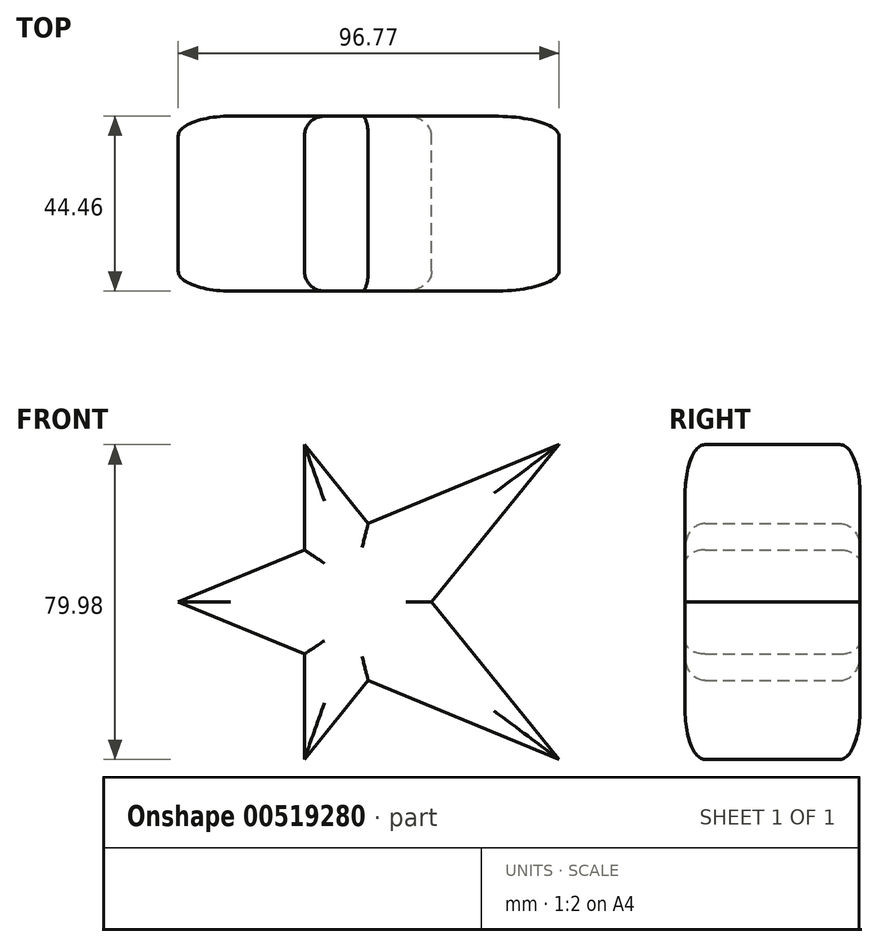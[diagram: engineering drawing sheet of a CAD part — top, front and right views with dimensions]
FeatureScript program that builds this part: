
annotation { "Feature Type Name" : "Feature", "Feature Type Description" : "" }
export const myFeature = defineFeature(function(context is Context, id is Id, definition is map)
    precondition{}
    {
        {
            var Q0;
            Q0=qCreatedBy(makeId("Front.planeOp"),FACE);
            var sketch = newSketch(context, id + "F0", { "sketchPlane" : qUnion([Q0])});
            skLineSegment(sketch, "E0", {"start": v(-48.54, 0) * mm, "end": v(48.23, 40) * mm});
            skLineSegment(sketch, "E1.MirrorCS", {"start": v(-48.54, 0) * mm, "end": v(48.23, -40) * mm});
            skLineSegment(sketch, "E2", {"start": v(-16.48, 40) * mm, "end": v(48.23, -40) * mm});
            skLineSegment(sketch, "E3", {"start": v(48.23, 40) * mm, "end": v(-16.48, -40) * mm});
            skLineSegment(sketch, "E4", {"start": v(-16.48, 40) * mm, "end": v(-16.48, -40) * mm});
            skSolve(sketch);
        }
        {
            var Q0;
            {var subQ5=sQuery(id+"F0.wireOp",EDGE,"E0");var subQ7=sQuery(id+"F0.wireOp",EDGE,"E4");var subQ9=makeQuery(id+"F0.imprint","INTERSECT",VERTEX,{"derivedFrom":[subQ5,subQ7]});Q0=makeQuery(id+"F0.imprint","IMPRINT",FACE,{"disambiguationData":[TD([[makeQuery(id+"F0.imprint","IMPRINT",EDGE,{"disambiguationData":[TD([[subQ9,-1.0]])],"derivedFrom":subQ5}),-1.0]])]});}
            var Q1;
            {var subQ0=sQuery(id+"F0.wireOp",EDGE,"E1.MirrorCS");var subQ1=sQuery(id+"F0.wireOp",EDGE,"E0");var subQ2=makeQuery(id+"F0.imprint","INTERSECT",VERTEX,{"derivedFrom":[subQ1,subQ0]});Q1=makeQuery(id+"F0.imprint","IMPRINT",FACE,{"disambiguationData":[TD([[makeQuery(id+"F0.imprint","IMPRINT",EDGE,{"disambiguationData":[TD([[subQ2,-1.0]])],"derivedFrom":subQ1}),-1.0]])]});}
            var Q2;
            {var subQ0=sQuery(id+"F0.wireOp",EDGE,"E4");var subQ1=sQuery(id+"F0.wireOp",EDGE,"E0");var subQ2=makeQuery(id+"F0.imprint","INTERSECT",VERTEX,{"derivedFrom":[subQ1,subQ0]});Q2=makeQuery(id+"F0.imprint","IMPRINT",FACE,{"disambiguationData":[TD([[makeQuery(id+"F0.imprint","IMPRINT",EDGE,{"disambiguationData":[TD([[subQ2,-1.0]])],"derivedFrom":subQ1}),1.0]])]});}
            var Q3;
            {var subQ0=sQuery(id+"F0.wireOp",EDGE,"E3");var subQ1=sQuery(id+"F0.wireOp",EDGE,"E0");var subQ2=makeQuery(id+"F0.imprint","INTERSECT",VERTEX,{"derivedFrom":[subQ1,subQ0]});Q3=makeQuery(id+"F0.imprint","IMPRINT",FACE,{"disambiguationData":[TD([[makeQuery(id+"F0.imprint","IMPRINT",EDGE,{"disambiguationData":[TD([[subQ2,1.0]])],"derivedFrom":subQ1}),-1.0]])]});}
            var Q4;
            {var subQ0=sQuery(id+"F0.wireOp",EDGE,"E2");var subQ1=sQuery(id+"F0.wireOp",EDGE,"E1.MirrorCS");var subQ2=makeQuery(id+"F0.imprint","INTERSECT",VERTEX,{"derivedFrom":[subQ1,subQ0]});Q4=makeQuery(id+"F0.imprint","IMPRINT",FACE,{"disambiguationData":[TD([[makeQuery(id+"F0.imprint","IMPRINT",EDGE,{"disambiguationData":[TD([[subQ2,1.0]])],"derivedFrom":subQ1}),1.0]])]});}
            var Q5;
            {var subQ0=sQuery(id+"F0.wireOp",EDGE,"E4");var subQ1=sQuery(id+"F0.wireOp",EDGE,"E1.MirrorCS");var subQ2=makeQuery(id+"F0.imprint","INTERSECT",VERTEX,{"derivedFrom":[subQ1,subQ0]});Q5=makeQuery(id+"F0.imprint","IMPRINT",FACE,{"disambiguationData":[TD([[makeQuery(id+"F0.imprint","IMPRINT",EDGE,{"disambiguationData":[TD([[subQ2,-1.0]])],"derivedFrom":subQ1}),-1.0]])]});}
            extrude(context, id + "F1", {"entities" : qUnion([Q0, Q1, Q2, Q3, Q4, Q5]), "endBound" : BoundingType.SYMMETRIC, "depth" : 44.45 * mm, "offsetDistance" : 25.4 * mm});
        }
        {
            var Q0;
            {var subQ0=sQuery(id+"F0.wireOp",EDGE,"E1.MirrorCS");Q0=makeQuery(id+"F1.opExtrude","CAP_EDGE",EDGE,{"disambiguationData":[OSD([subQ0]),TDD([makeQuery(id+"F0.imprint","IMPRINT",EDGE,{"disambiguationData":[TD([[makeQuery(id+"F0.imprint","INTERSECT",VERTEX,{"derivedFrom":[sQuery(id+"F0.wireOp",EDGE,"E0"),subQ0]}),-1.0]])],"derivedFrom":subQ0})])],"isStart":false});}
            var Q1;
            {var subQ0=sQuery(id+"F0.wireOp",EDGE,"E4");Q1=makeQuery(id+"F1.opExtrude","CAP_EDGE",EDGE,{"disambiguationData":[OSD([subQ0]),TDD([makeQuery(id+"F0.imprint","IMPRINT",EDGE,{"disambiguationData":[TD([[makeQuery(id+"F0.imprint","INTERSECT",VERTEX,{"derivedFrom":[sQuery(id+"F0.wireOp",EDGE,"E3"),subQ0]}),1.0]])],"derivedFrom":subQ0})])],"isStart":false});}
            var Q2;
            {var subQ0=sQuery(id+"F0.wireOp",EDGE,"E3");Q2=makeQuery(id+"F1.opExtrude","CAP_EDGE",EDGE,{"disambiguationData":[OSD([subQ0]),TDD([makeQuery(id+"F0.imprint","IMPRINT",EDGE,{"disambiguationData":[TD([[makeQuery(id+"F0.imprint","INTERSECT",VERTEX,{"derivedFrom":[subQ0,sQuery(id+"F0.wireOp",EDGE,"E4")]}),1.0]])],"derivedFrom":subQ0})])],"isStart":false});}
            var Q3;
            {var subQ0=sQuery(id+"F0.wireOp",EDGE,"E1.MirrorCS");Q3=makeQuery(id+"F1.opExtrude","CAP_EDGE",EDGE,{"disambiguationData":[OSD([subQ0]),TDD([makeQuery(id+"F0.imprint","IMPRINT",EDGE,{"disambiguationData":[TD([[makeQuery(id+"F0.imprint","INTERSECT",VERTEX,{"derivedFrom":[subQ0,sQuery(id+"F0.wireOp",EDGE,"E2")]}),1.0]])],"derivedFrom":subQ0})])],"isStart":false});}
            var Q4;
            {var subQ0=sQuery(id+"F0.wireOp",EDGE,"E2");Q4=makeQuery(id+"F1.opExtrude","CAP_EDGE",EDGE,{"disambiguationData":[OSD([subQ0]),TDD([makeQuery(id+"F0.imprint","IMPRINT",EDGE,{"disambiguationData":[TD([[makeQuery(id+"F0.imprint","INTERSECT",VERTEX,{"derivedFrom":[sQuery(id+"F0.wireOp",EDGE,"E1.MirrorCS"),subQ0]}),1.0]])],"derivedFrom":subQ0})])],"isStart":false});}
            var Q5;
            {var subQ0=sQuery(id+"F0.wireOp",EDGE,"E3");Q5=makeQuery(id+"F1.opExtrude","CAP_EDGE",EDGE,{"disambiguationData":[OSD([subQ0]),TDD([makeQuery(id+"F0.imprint","IMPRINT",EDGE,{"disambiguationData":[TD([[makeQuery(id+"F0.imprint","INTERSECT",VERTEX,{"derivedFrom":[sQuery(id+"F0.wireOp",EDGE,"E0"),subQ0]}),-1.0]])],"derivedFrom":subQ0})])],"isStart":false});}
            var Q6;
            {var subQ0=sQuery(id+"F0.wireOp",EDGE,"E0");Q6=makeQuery(id+"F1.opExtrude","CAP_EDGE",EDGE,{"disambiguationData":[OSD([subQ0]),TDD([makeQuery(id+"F0.imprint","IMPRINT",EDGE,{"disambiguationData":[TD([[makeQuery(id+"F0.imprint","INTERSECT",VERTEX,{"derivedFrom":[subQ0,sQuery(id+"F0.wireOp",EDGE,"E3")]}),1.0]])],"derivedFrom":subQ0})])],"isStart":false});}
            var Q7;
            {var subQ0=sQuery(id+"F0.wireOp",EDGE,"E2");Q7=makeQuery(id+"F1.opExtrude","CAP_EDGE",EDGE,{"disambiguationData":[OSD([subQ0]),TDD([makeQuery(id+"F0.imprint","IMPRINT",EDGE,{"disambiguationData":[TD([[makeQuery(id+"F0.imprint","INTERSECT",VERTEX,{"derivedFrom":[subQ0,sQuery(id+"F0.wireOp",EDGE,"E4")]}),-1.0]])],"derivedFrom":subQ0})])],"isStart":false});}
            var Q8;
            {var subQ0=sQuery(id+"F0.wireOp",EDGE,"E4");Q8=makeQuery(id+"F1.opExtrude","CAP_EDGE",EDGE,{"disambiguationData":[OSD([subQ0]),TDD([makeQuery(id+"F0.imprint","IMPRINT",EDGE,{"disambiguationData":[TD([[makeQuery(id+"F0.imprint","INTERSECT",VERTEX,{"derivedFrom":[sQuery(id+"F0.wireOp",EDGE,"E2"),subQ0]}),-1.0]])],"derivedFrom":subQ0})])],"isStart":false});}
            var Q9;
            {var subQ0=sQuery(id+"F0.wireOp",EDGE,"E0");Q9=makeQuery(id+"F1.opExtrude","CAP_EDGE",EDGE,{"disambiguationData":[OSD([subQ0]),TDD([makeQuery(id+"F0.imprint","IMPRINT",EDGE,{"disambiguationData":[TD([[makeQuery(id+"F0.imprint","INTERSECT",VERTEX,{"derivedFrom":[subQ0,sQuery(id+"F0.wireOp",EDGE,"E1.MirrorCS")]}),-1.0]])],"derivedFrom":subQ0})])],"isStart":false});}
            var Q10;
            {var subQ0=sQuery(id+"F0.wireOp",EDGE,"E0");Q10=makeQuery(id+"F1.opExtrude","CAP_EDGE",EDGE,{"disambiguationData":[OSD([subQ0]),TDD([makeQuery(id+"F0.imprint","IMPRINT",EDGE,{"disambiguationData":[TD([[makeQuery(id+"F0.imprint","INTERSECT",VERTEX,{"derivedFrom":[subQ0,sQuery(id+"F0.wireOp",EDGE,"E1.MirrorCS")]}),-1.0]])],"derivedFrom":subQ0})])],"isStart":true});}
            var Q11;
            {var subQ0=sQuery(id+"F0.wireOp",EDGE,"E4");Q11=makeQuery(id+"F1.opExtrude","CAP_EDGE",EDGE,{"disambiguationData":[OSD([subQ0]),TDD([makeQuery(id+"F0.imprint","IMPRINT",EDGE,{"disambiguationData":[TD([[makeQuery(id+"F0.imprint","INTERSECT",VERTEX,{"derivedFrom":[sQuery(id+"F0.wireOp",EDGE,"E2"),subQ0]}),-1.0]])],"derivedFrom":subQ0})])],"isStart":true});}
            var Q12;
            {var subQ0=sQuery(id+"F0.wireOp",EDGE,"E2");Q12=makeQuery(id+"F1.opExtrude","CAP_EDGE",EDGE,{"disambiguationData":[OSD([subQ0]),TDD([makeQuery(id+"F0.imprint","IMPRINT",EDGE,{"disambiguationData":[TD([[makeQuery(id+"F0.imprint","INTERSECT",VERTEX,{"derivedFrom":[subQ0,sQuery(id+"F0.wireOp",EDGE,"E4")]}),-1.0]])],"derivedFrom":subQ0})])],"isStart":true});}
            var Q13;
            {var subQ0=sQuery(id+"F0.wireOp",EDGE,"E0");Q13=makeQuery(id+"F1.opExtrude","CAP_EDGE",EDGE,{"disambiguationData":[OSD([subQ0]),TDD([makeQuery(id+"F0.imprint","IMPRINT",EDGE,{"disambiguationData":[TD([[makeQuery(id+"F0.imprint","INTERSECT",VERTEX,{"derivedFrom":[subQ0,sQuery(id+"F0.wireOp",EDGE,"E3")]}),1.0]])],"derivedFrom":subQ0})])],"isStart":true});}
            var Q14;
            {var subQ0=sQuery(id+"F0.wireOp",EDGE,"E3");Q14=makeQuery(id+"F1.opExtrude","CAP_EDGE",EDGE,{"disambiguationData":[OSD([subQ0]),TDD([makeQuery(id+"F0.imprint","IMPRINT",EDGE,{"disambiguationData":[TD([[makeQuery(id+"F0.imprint","INTERSECT",VERTEX,{"derivedFrom":[sQuery(id+"F0.wireOp",EDGE,"E0"),subQ0]}),-1.0]])],"derivedFrom":subQ0})])],"isStart":true});}
            var Q15;
            {var subQ0=sQuery(id+"F0.wireOp",EDGE,"E2");Q15=makeQuery(id+"F1.opExtrude","CAP_EDGE",EDGE,{"disambiguationData":[OSD([subQ0]),TDD([makeQuery(id+"F0.imprint","IMPRINT",EDGE,{"disambiguationData":[TD([[makeQuery(id+"F0.imprint","INTERSECT",VERTEX,{"derivedFrom":[sQuery(id+"F0.wireOp",EDGE,"E1.MirrorCS"),subQ0]}),1.0]])],"derivedFrom":subQ0})])],"isStart":true});}
            var Q16;
            {var subQ0=sQuery(id+"F0.wireOp",EDGE,"E1.MirrorCS");Q16=makeQuery(id+"F1.opExtrude","CAP_EDGE",EDGE,{"disambiguationData":[OSD([subQ0]),TDD([makeQuery(id+"F0.imprint","IMPRINT",EDGE,{"disambiguationData":[TD([[makeQuery(id+"F0.imprint","INTERSECT",VERTEX,{"derivedFrom":[subQ0,sQuery(id+"F0.wireOp",EDGE,"E2")]}),1.0]])],"derivedFrom":subQ0})])],"isStart":true});}
            var Q17;
            {var subQ0=sQuery(id+"F0.wireOp",EDGE,"E3");Q17=makeQuery(id+"F1.opExtrude","CAP_EDGE",EDGE,{"disambiguationData":[OSD([subQ0]),TDD([makeQuery(id+"F0.imprint","IMPRINT",EDGE,{"disambiguationData":[TD([[makeQuery(id+"F0.imprint","INTERSECT",VERTEX,{"derivedFrom":[subQ0,sQuery(id+"F0.wireOp",EDGE,"E4")]}),1.0]])],"derivedFrom":subQ0})])],"isStart":true});}
            var Q18;
            {var subQ0=sQuery(id+"F0.wireOp",EDGE,"E4");Q18=makeQuery(id+"F1.opExtrude","CAP_EDGE",EDGE,{"disambiguationData":[OSD([subQ0]),TDD([makeQuery(id+"F0.imprint","IMPRINT",EDGE,{"disambiguationData":[TD([[makeQuery(id+"F0.imprint","INTERSECT",VERTEX,{"derivedFrom":[sQuery(id+"F0.wireOp",EDGE,"E3"),subQ0]}),1.0]])],"derivedFrom":subQ0})])],"isStart":true});}
            var Q19;
            {var subQ0=sQuery(id+"F0.wireOp",EDGE,"E1.MirrorCS");Q19=makeQuery(id+"F1.opExtrude","CAP_EDGE",EDGE,{"disambiguationData":[OSD([subQ0]),TDD([makeQuery(id+"F0.imprint","IMPRINT",EDGE,{"disambiguationData":[TD([[makeQuery(id+"F0.imprint","INTERSECT",VERTEX,{"derivedFrom":[sQuery(id+"F0.wireOp",EDGE,"E0"),subQ0]}),-1.0]])],"derivedFrom":subQ0})])],"isStart":true});}
            fillet(context, id + "F2", {"entities" : qUnion([Q0, Q1, Q2, Q3, Q4, Q5, Q6, Q7, Q8, Q9, Q10, Q11, Q12, Q13, Q14, Q15, Q16, Q17, Q18, Q19]), "radius" : 5.08 * mm, "tangentPropagation" : true, "allowEdgeOverflow" : false});
        }
    });
